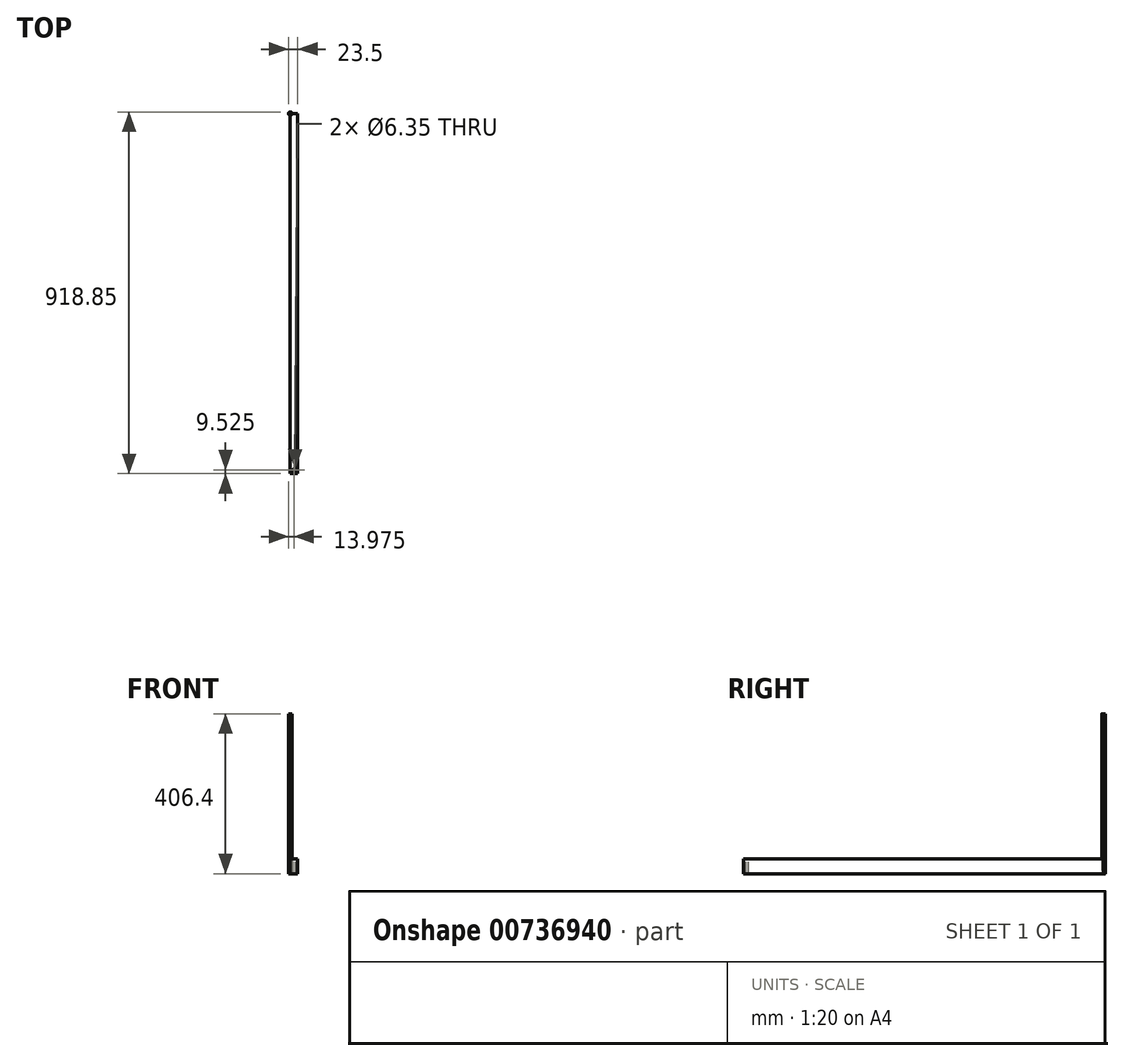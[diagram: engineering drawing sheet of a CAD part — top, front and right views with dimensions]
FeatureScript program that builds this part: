
annotation { "Feature Type Name" : "Feature", "Feature Type Description" : "" }
export const myFeature = defineFeature(function(context is Context, id is Id, definition is map)
    precondition{}
    {
        {
            var Q0;
            Q0=qCreatedBy(makeId("Front.planeOp"),FACE);
            var sketch = newSketch(context, id + "F0", { "sketchPlane" : qUnion([Q0])});
            skLineSegment(sketch, "E0.bottom", {"start": v(0, 0) * mm, "end": v(19.05, 0) * mm});
            skLineSegment(sketch, "E0.top", {"start": v(0, 38.1) * mm, "end": v(19.05, 38.1) * mm});
            skLineSegment(sketch, "E0.left", {"start": v(0, 0) * mm, "end": v(0, 38.1) * mm});
            skLineSegment(sketch, "E0.right", {"start": v(19.05, 0) * mm, "end": v(19.05, 38.1) * mm});
            skSolve(sketch);
        }
        {
            var Q0;
            Q0 = qSketchRegion(id + "F0", true);
            extrude(context, id + "F1", {"entities" : qUnion([Q0]), "depth" : 914.4 * mm, "offsetDistance" : 25.4 * mm});
        }
        {
            var Q0;
            Q0=qCreatedBy(makeId("Top.planeOp"),FACE);
            var sketch = newSketch(context, id + "F2", { "sketchPlane" : qUnion([Q0])});
            skCircle(sketch, "E1", {"center": v(0, 0) * mm, "radius": 4.45 * mm});
            skSolve(sketch);
        }
        {
            var Q0;
            Q0=makeQuery(id+"F2.imprint","IMPRINT",FACE,{"disambiguationData":[TD([[makeQuery(id+"F2.imprint","IMPRINT",EDGE,{"derivedFrom":sQuery(id+"F2.wireOp",EDGE,"E1")}),1.0]])]});
            extrude(context, id + "F3", {"entities" : qUnion([Q0]), "depth" : 406.4 * mm, "offsetDistance" : 25.4 * mm});
        }
        {
            var Q0;
            Q0=makeQuery(id+"F1.opExtrude","SWEPT_FACE",FACE,{"disambiguationData":[OSD([sQuery(id+"F0.wireOp",EDGE,"E0.top")])]});
            var sketch = newSketch(context, id + "F4", { "sketchPlane" : qUnion([Q0])});
            skCircle(sketch, "E2", {"center": v(9.52, -904.88) * mm, "radius": 3.18 * mm});
            skPoint(sketch, "E2.centerSnap0", {"position": v(9.53, -914.4) * mm});
            skCircle(sketch, "E3", {"center": v(9.52, -904.88) * mm, "radius": 9.52 * mm});
            skSolve(sketch);
        }
        {
            var Q0;
            {var subQ0=sQuery(id+"F4.wireOp",EDGE,"E3");var subQ1=sQuery(id+"F0.wireOp",EDGE,"E0.top");var subQ4=makeQuery(id+"F1.opExtrude","CAP_EDGE",EDGE,{"disambiguationData":[OSD([subQ1])],"isStart":false});var subQ5=makeQuery(id+"F4.imprint","INTERSECT",VERTEX,{"derivedFrom":[subQ4,subQ0]});Q0=makeQuery(id+"F4.imprint","IMPRINT",FACE,{"disambiguationData":[TD([[makeQuery(id+"F4.imprint","IMPRINT",EDGE,{"disambiguationData":[TD([[subQ5,1.0]])],"derivedFrom":subQ0}),-1.0]])]});}
            var Q1;
            {var subQ0=sQuery(id+"F4.wireOp",EDGE,"E3");var subQ1=sQuery(id+"F0.wireOp",EDGE,"E0.top");var subQ4=makeQuery(id+"F1.opExtrude","CAP_EDGE",EDGE,{"disambiguationData":[OSD([subQ1])],"isStart":false});var subQ5=makeQuery(id+"F4.imprint","INTERSECT",VERTEX,{"derivedFrom":[subQ4,subQ0]});Q1=makeQuery(id+"F4.imprint","IMPRINT",FACE,{"disambiguationData":[TD([[makeQuery(id+"F4.imprint","IMPRINT",EDGE,{"disambiguationData":[TD([[subQ5,-1.0]])],"derivedFrom":subQ0}),-1.0]])]});}
            var Q2;
            Q2=makeQuery(id+"F4.imprint","IMPRINT",FACE,{"disambiguationData":[TD([[makeQuery(id+"F4.imprint","IMPRINT",EDGE,{"derivedFrom":sQuery(id+"F4.wireOp",EDGE,"E2")}),1.0]])]});
            extrude(context, id + "F5", {"entities" : qUnion([Q0, Q1, Q2]), "operationType" : NewBodyOperationType.REMOVE, "endBound" : BoundingType.THROUGH_ALL, "oppositeDirection" : true, "depth" : 25.4 * mm, "offsetDistance" : 25.4 * mm});
        }
        {
            var Q0;
            Q0=makeQuery(id+"F0.imprint","IMPRINT",FACE,{"disambiguationData":[TD([[makeQuery(id+"F0.imprint","IMPRINT",EDGE,{"derivedFrom":sQuery(id+"F0.wireOp",EDGE,"E0.bottom")}),1.0]])]});
            extrude(context, id + "F6", {"entities" : qUnion([Q0]), "depth" : 914.4 * mm, "offsetDistance" : 25.4 * mm});
        }
        {
            var Q0;
            Q0=makeQuery(id+"F4.imprint","IMPRINT",FACE,{"disambiguationData":[TD([[makeQuery(id+"F4.imprint","IMPRINT",EDGE,{"derivedFrom":sQuery(id+"F4.wireOp",EDGE,"E2")}),1.0]])]});
            var Q1;
            Q1=sQuery(id+"F4.wireOp",EDGE,"E2");
            extrude(context, id + "F7", {"entities" : qUnion([Q0]), "operationType" : NewBodyOperationType.REMOVE, "surfaceEntities" : qUnion([Q1]), "endBound" : BoundingType.THROUGH_ALL, "oppositeDirection" : true, "depth" : 25.4 * mm, "offsetDistance" : 25.4 * mm});
        }
    });
